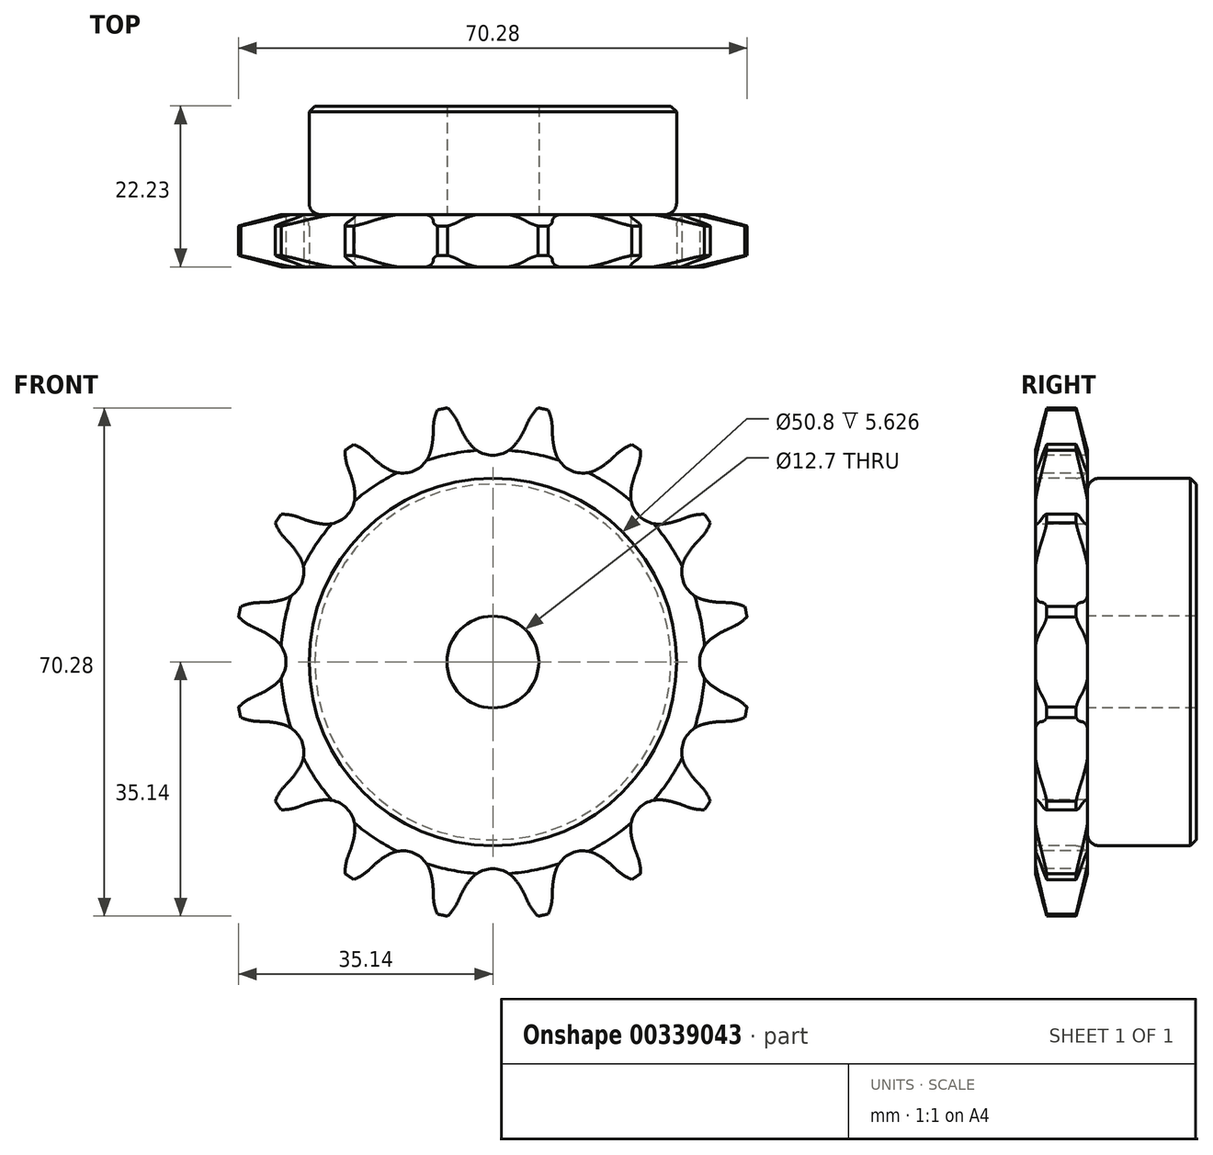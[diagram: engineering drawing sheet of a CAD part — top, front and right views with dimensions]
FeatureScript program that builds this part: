
annotation { "Feature Type Name" : "Feature", "Feature Type Description" : "" }
export const myFeature = defineFeature(function(context is Context, id is Id, definition is map)
    precondition{}
    {
        {
            var Q0;
            Q0=qCreatedBy(makeId("Right.planeOp"),FACE);
            var sketch = newSketch(context, id + "F0", { "sketchPlane" : qUnion([Q0])});
            skLineSegment(sketch, "E0", {"start": v(0, 0) * mm, "end": v(22.23, 0) * mm});
            skLineSegment(sketch, "E1.bottom", {"start": v(0, 6.35) * mm, "end": v(7.21, 6.35) * mm});
            skLineSegment(sketch, "E1.top", {"start": v(0, 35.69) * mm, "end": v(7.21, 35.69) * mm});
            skLineSegment(sketch, "E1.left", {"start": v(0, 6.35) * mm, "end": v(0, 35.69) * mm});
            skLineSegment(sketch, "E1.right", {"start": v(7.21, 6.35) * mm, "end": v(7.21, 35.69) * mm});
            skLineSegment(sketch, "E2.bottom", {"start": v(0, 6.35) * mm, "end": v(22.23, 6.35) * mm});
            skLineSegment(sketch, "E2.top", {"start": v(0, 25.4) * mm, "end": v(22.23, 25.4) * mm});
            skLineSegment(sketch, "E2.left", {"start": v(0, 6.35) * mm, "end": v(0, 25.4) * mm});
            skLineSegment(sketch, "E2.right", {"start": v(22.23, 6.35) * mm, "end": v(22.22, 25.4) * mm});
            skLineSegment(sketch, "E3.MirrorCS", {"start": v(0, -6.35) * mm, "end": v(7.21, -6.35) * mm});
            skLineSegment(sketch, "E4.MirrorCS", {"start": v(0, -25.4) * mm, "end": v(22.23, -25.4) * mm});
            skLineSegment(sketch, "E5.MirrorCS", {"start": v(0, -6.35) * mm, "end": v(22.23, -6.35) * mm});
            skLineSegment(sketch, "E6.MirrorCS", {"start": v(22.23, -6.35) * mm, "end": v(22.23, -25.4) * mm});
            skLineSegment(sketch, "E7.MirrorCS", {"start": v(7.21, -6.35) * mm, "end": v(7.21, -35.69) * mm});
            skLineSegment(sketch, "E8.MirrorCS", {"start": v(0, -6.35) * mm, "end": v(0, -35.69) * mm});
            skLineSegment(sketch, "E9.MirrorCS", {"start": v(0, -35.69) * mm, "end": v(7.21, -35.69) * mm});
            skLineSegment(sketch, "E10.MirrorCS", {"start": v(0, -6.35) * mm, "end": v(0, -25.4) * mm});
            skSolve(sketch);
        }
        {
            var Q0;
            {var subQ5=sQuery(id+"F0.wireOp",EDGE,"E2.right");Q0=makeQuery(id+"F0.imprint","IMPRINT",FACE,{"disambiguationData":[TD([[makeQuery(id+"F0.imprint","IMPRINT",EDGE,{"derivedFrom":subQ5}),1.0]])]});}
            var Q1;
            {var subQ5=sQuery(id+"F0.wireOp",EDGE,"E2.left");Q1=makeQuery(id+"F0.imprint","IMPRINT",FACE,{"disambiguationData":[TD([[makeQuery(id+"F0.imprint","IMPRINT",EDGE,{"derivedFrom":subQ5}),-1.0]])]});}
            var Q2;
            {var subQ0=sQuery(id+"F0.wireOp",EDGE,"E1.top");Q2=makeQuery(id+"F0.imprint","IMPRINT",FACE,{"disambiguationData":[TD([[makeQuery(id+"F0.imprint","IMPRINT",EDGE,{"derivedFrom":subQ0}),-1.0]])]});}
            var Q3;
            Q3=sQuery(id+"F0.wireOp",EDGE,"E0");
            revolve(context, id + "F1", {"entities" : qUnion([Q0, Q1, Q2]), "axis" : qUnion([Q3]), "revolveType" : RevolveType.FULL});
        }
        {
            var Q0;
            Q0=makeQuery(id+"F1.opRevolve","SWEPT_EDGE",EDGE,{"disambiguationData":[OSD([sQuery(id+"F0.wireOp",EDGE,"E1.right"),sQuery(id+"F0.wireOp",EDGE,"E2.top")])]});
            fillet(context, id + "F2", {"entities" : qUnion([Q0]), "radius" : 1.59 * mm, "tangentPropagation" : true, "allowEdgeOverflow" : false});
        }
        {
            var Q0;
            Q0=makeQuery(id+"F1.opRevolve","SWEPT_EDGE",EDGE,{"disambiguationData":[OSD([sQuery(id+"F0.wireOp",EDGE,"E2.top"),sQuery(id+"F0.wireOp",EDGE,"E2.right")])]});
            chamfer(context, id + "F3", {"entities" : qUnion([Q0]), "width" : 0.8 * mm, "tangentPropagation" : true});
        }
        {
            var Q0;
            Q0=makeQuery(id+"F1.opRevolve","SWEPT_EDGE",EDGE,{"disambiguationData":[OSD([sQuery(id+"F0.wireOp",EDGE,"E1.top"),sQuery(id+"F0.wireOp",EDGE,"E1.left")])]});
            var Q1;
            Q1=makeQuery(id+"F1.opRevolve","SWEPT_EDGE",EDGE,{"disambiguationData":[OSD([sQuery(id+"F0.wireOp",EDGE,"E1.top"),sQuery(id+"F0.wireOp",EDGE,"E1.right")])]});
            chamfer(context, id + "F4", {"entities" : qUnion([Q0, Q1]), "chamferType" : ChamferType.TWO_OFFSETS, "width1" : 6.35 * mm, "oppositeDirection" : false, "width2" : 1.57 * mm, "tangentPropagation" : true});
        }
        {
            var Q0;
            Q0=makeQuery(id+"F1.opRevolve","SWEPT_FACE",FACE,{"disambiguationData":[OSD([sQuery(id+"F0.wireOp",EDGE,"E1.left"),sQuery(id+"F0.wireOp",EDGE,"E2.left")])]});
            var sketch = newSketch(context, id + "F5", { "sketchPlane" : qUnion([Q0])});
            skCircle(sketch, "E11", {"center": v(0, 0) * mm, "radius": 32.55 * mm, "construction": true});
            skLineSegment(sketch, "E12", {"start": v(0, 0) * mm, "end": v(0, 32.55) * mm, "construction": true});
            skLineSegment(sketch, "E13", {"start": v(47.22, 32.55) * mm, "end": v(0, 32.55) * mm, "construction": true});
            skLineSegment(sketch, "E14", {"start": v(0, 32.55) * mm, "end": v(5, 36.56) * mm, "construction": true});
            skLineSegment(sketch, "E15", {"start": v(5, 36.56) * mm, "end": v(-4.46, 32.3) * mm, "construction": true});
            skLineSegment(sketch, "E16", {"start": v(-4.46, 32.3) * mm, "end": v(-4.82, 33.1) * mm});
            skLineSegment(sketch, "E17", {"start": v(0, 0) * mm, "end": v(-7.13, 35.85) * mm, "construction": true});
            skArc(sketch, "E18", {"start": v(-7.13, 35.85) * mm, "mid": v(-15.87, 26.15) * mm, "end": v(-4.82, 33.1) * mm, "construction": true});
            skArc(sketch, "E19", {"start": v(-4.82, 33.1) * mm, "mid": v(-5.78, 34.63) * mm, "end": v(-7.13, 35.85) * mm});
            skLineSegment(sketch, "E20", {"start": v(-4.82, 33.1) * mm, "end": v(-4.82, 33.1) * mm});
            skLineSegment(sketch, "E21", {"start": v(-4.46, 32.3) * mm, "end": v(-4.46, 32.3) * mm});
            skArc(sketch, "E22", {"start": v(-3.1, 30.07) * mm, "mid": v(13.83, 41.97) * mm, "end": v(-4.46, 32.3) * mm, "construction": true});
            skArc(sketch, "E23.MirrorCS", {"start": v(4.82, 33.1) * mm, "mid": v(5.78, 34.63) * mm, "end": v(7.13, 35.85) * mm});
            skArc(sketch, "E24.MirrorCS", {"start": v(4.46, 32.3) * mm, "mid": v(3.84, 31.14) * mm, "end": v(3.1, 30.07) * mm});
            skArc(sketch, "E25", {"start": v(-4.46, 32.3) * mm, "mid": v(-3.84, 31.14) * mm, "end": v(-3.1, 30.07) * mm});
            skLineSegment(sketch, "E26", {"start": v(-4.82, 33.1) * mm, "end": v(-11.63, 48.22) * mm, "construction": true});
            skLineSegment(sketch, "E27.MirrorCS", {"start": v(4.46, 32.3) * mm, "end": v(4.82, 33.1) * mm});
            skArc(sketch, "E28", {"start": v(3.1, 30.07) * mm, "mid": v(0, 36.51) * mm, "end": v(-3.1, 30.07) * mm, "construction": true});
            skArc(sketch, "E29", {"start": v(-3.1, 30.07) * mm, "mid": v(0, 28.59) * mm, "end": v(3.1, 30.07) * mm});
            skLineSegment(sketch, "E30.1.0", {"start": v(-16.48, 28.14) * mm, "end": v(-17.12, 28.74) * mm});
            skArc(sketch, "E30.1.1", {"start": v(-17.12, 28.74) * mm, "mid": v(-18.6, 29.79) * mm, "end": v(-20.3, 30.4) * mm});
            skArc(sketch, "E30.1.2", {"start": v(-14.36, 26.6) * mm, "mid": v(-10.94, 26.41) * mm, "end": v(-8.65, 28.96) * mm});
            skArc(sketch, "E30.1.3", {"start": v(-16.48, 28.14) * mm, "mid": v(-15.47, 27.3) * mm, "end": v(-14.36, 26.6) * mm});
            skArc(sketch, "E30.1.4", {"start": v(-8.24, 31.55) * mm, "mid": v(-8.37, 30.24) * mm, "end": v(-8.65, 28.96) * mm});
            skLineSegment(sketch, "E30.1.5", {"start": v(-8.24, 31.55) * mm, "end": v(-8.22, 32.42) * mm});
            skArc(sketch, "E30.1.6", {"start": v(-8.22, 32.42) * mm, "mid": v(-7.91, 34.21) * mm, "end": v(-7.13, 35.85) * mm});
            skLineSegment(sketch, "E30.2.0", {"start": v(-26, 19.69) * mm, "end": v(-26.8, 20) * mm});
            skArc(sketch, "E30.2.1", {"start": v(-26.8, 20) * mm, "mid": v(-28.58, 20.4) * mm, "end": v(-30.4, 20.3) * mm});
            skArc(sketch, "E30.2.2", {"start": v(-23.45, 19.08) * mm, "mid": v(-20.21, 20.21) * mm, "end": v(-19.08, 23.45) * mm});
            skArc(sketch, "E30.2.3", {"start": v(-26, 19.69) * mm, "mid": v(-24.74, 19.3) * mm, "end": v(-23.45, 19.08) * mm});
            skArc(sketch, "E30.2.4", {"start": v(-19.69, 26) * mm, "mid": v(-19.3, 24.74) * mm, "end": v(-19.08, 23.45) * mm});
            skLineSegment(sketch, "E30.2.5", {"start": v(-19.69, 26) * mm, "end": v(-20, 26.8) * mm});
            skArc(sketch, "E30.2.6", {"start": v(-20, 26.8) * mm, "mid": v(-20.4, 28.58) * mm, "end": v(-20.3, 30.4) * mm});
            skLineSegment(sketch, "E30.3.0", {"start": v(-31.55, 8.24) * mm, "end": v(-32.42, 8.22) * mm});
            skArc(sketch, "E30.3.1", {"start": v(-32.42, 8.22) * mm, "mid": v(-34.21, 7.91) * mm, "end": v(-35.85, 7.13) * mm});
            skArc(sketch, "E30.3.2", {"start": v(-28.96, 8.65) * mm, "mid": v(-26.41, 10.94) * mm, "end": v(-26.6, 14.36) * mm});
            skArc(sketch, "E30.3.3", {"start": v(-31.55, 8.24) * mm, "mid": v(-30.24, 8.37) * mm, "end": v(-28.96, 8.65) * mm});
            skArc(sketch, "E30.3.4", {"start": v(-28.14, 16.48) * mm, "mid": v(-27.3, 15.47) * mm, "end": v(-26.6, 14.36) * mm});
            skLineSegment(sketch, "E30.3.5", {"start": v(-28.14, 16.48) * mm, "end": v(-28.74, 17.12) * mm});
            skArc(sketch, "E30.3.6", {"start": v(-28.74, 17.12) * mm, "mid": v(-29.79, 18.6) * mm, "end": v(-30.4, 20.3) * mm});
            skLineSegment(sketch, "E30.4.0", {"start": v(-32.3, -4.46) * mm, "end": v(-33.1, -4.82) * mm});
            skArc(sketch, "E30.4.1", {"start": v(-33.1, -4.82) * mm, "mid": v(-34.63, -5.78) * mm, "end": v(-35.85, -7.13) * mm});
            skArc(sketch, "E30.4.2", {"start": v(-30.07, -3.1) * mm, "mid": v(-28.59, 0) * mm, "end": v(-30.07, 3.1) * mm});
            skArc(sketch, "E30.4.3", {"start": v(-32.3, -4.46) * mm, "mid": v(-31.14, -3.84) * mm, "end": v(-30.07, -3.1) * mm});
            skArc(sketch, "E30.4.4", {"start": v(-32.3, 4.46) * mm, "mid": v(-31.14, 3.84) * mm, "end": v(-30.07, 3.1) * mm});
            skLineSegment(sketch, "E30.4.5", {"start": v(-32.3, 4.46) * mm, "end": v(-33.1, 4.82) * mm});
            skArc(sketch, "E30.4.6", {"start": v(-33.1, 4.82) * mm, "mid": v(-34.63, 5.78) * mm, "end": v(-35.85, 7.13) * mm});
            skLineSegment(sketch, "E30.5.0", {"start": v(-28.14, -16.48) * mm, "end": v(-28.74, -17.12) * mm});
            skArc(sketch, "E30.5.1", {"start": v(-28.74, -17.12) * mm, "mid": v(-29.79, -18.6) * mm, "end": v(-30.4, -20.3) * mm});
            skArc(sketch, "E30.5.2", {"start": v(-26.6, -14.36) * mm, "mid": v(-26.41, -10.94) * mm, "end": v(-28.96, -8.65) * mm});
            skArc(sketch, "E30.5.3", {"start": v(-28.14, -16.48) * mm, "mid": v(-27.3, -15.47) * mm, "end": v(-26.6, -14.36) * mm});
            skArc(sketch, "E30.5.4", {"start": v(-31.55, -8.24) * mm, "mid": v(-30.24, -8.37) * mm, "end": v(-28.96, -8.65) * mm});
            skLineSegment(sketch, "E30.5.5", {"start": v(-31.55, -8.24) * mm, "end": v(-32.42, -8.22) * mm});
            skArc(sketch, "E30.5.6", {"start": v(-32.42, -8.22) * mm, "mid": v(-34.21, -7.91) * mm, "end": v(-35.85, -7.13) * mm});
            skLineSegment(sketch, "E30.6.0", {"start": v(-19.69, -26) * mm, "end": v(-20, -26.8) * mm});
            skArc(sketch, "E30.6.1", {"start": v(-20, -26.8) * mm, "mid": v(-20.4, -28.58) * mm, "end": v(-20.3, -30.4) * mm});
            skArc(sketch, "E30.6.2", {"start": v(-19.08, -23.45) * mm, "mid": v(-20.21, -20.21) * mm, "end": v(-23.45, -19.08) * mm});
            skArc(sketch, "E30.6.3", {"start": v(-19.69, -26) * mm, "mid": v(-19.3, -24.74) * mm, "end": v(-19.08, -23.45) * mm});
            skArc(sketch, "E30.6.4", {"start": v(-26, -19.69) * mm, "mid": v(-24.74, -19.3) * mm, "end": v(-23.45, -19.08) * mm});
            skLineSegment(sketch, "E30.6.5", {"start": v(-26, -19.69) * mm, "end": v(-26.8, -20) * mm});
            skArc(sketch, "E30.6.6", {"start": v(-26.8, -20) * mm, "mid": v(-28.58, -20.4) * mm, "end": v(-30.4, -20.3) * mm});
            skLineSegment(sketch, "E30.7.0", {"start": v(-8.24, -31.55) * mm, "end": v(-8.22, -32.42) * mm});
            skArc(sketch, "E30.7.1", {"start": v(-8.22, -32.42) * mm, "mid": v(-7.91, -34.21) * mm, "end": v(-7.13, -35.85) * mm});
            skArc(sketch, "E30.7.2", {"start": v(-8.65, -28.96) * mm, "mid": v(-10.94, -26.41) * mm, "end": v(-14.36, -26.6) * mm});
            skArc(sketch, "E30.7.3", {"start": v(-8.24, -31.55) * mm, "mid": v(-8.37, -30.24) * mm, "end": v(-8.65, -28.96) * mm});
            skArc(sketch, "E30.7.4", {"start": v(-16.48, -28.14) * mm, "mid": v(-15.47, -27.3) * mm, "end": v(-14.36, -26.6) * mm});
            skLineSegment(sketch, "E30.7.5", {"start": v(-16.48, -28.14) * mm, "end": v(-17.12, -28.74) * mm});
            skArc(sketch, "E30.7.6", {"start": v(-17.12, -28.74) * mm, "mid": v(-18.6, -29.79) * mm, "end": v(-20.3, -30.4) * mm});
            skLineSegment(sketch, "E30.8.0", {"start": v(4.46, -32.3) * mm, "end": v(4.82, -33.1) * mm});
            skArc(sketch, "E30.8.1", {"start": v(4.82, -33.1) * mm, "mid": v(5.78, -34.63) * mm, "end": v(7.13, -35.85) * mm});
            skArc(sketch, "E30.8.2", {"start": v(3.1, -30.07) * mm, "mid": v(0, -28.59) * mm, "end": v(-3.1, -30.07) * mm});
            skArc(sketch, "E30.8.3", {"start": v(4.46, -32.3) * mm, "mid": v(3.84, -31.14) * mm, "end": v(3.1, -30.07) * mm});
            skArc(sketch, "E30.8.4", {"start": v(-4.46, -32.3) * mm, "mid": v(-3.84, -31.14) * mm, "end": v(-3.1, -30.07) * mm});
            skLineSegment(sketch, "E30.8.5", {"start": v(-4.46, -32.3) * mm, "end": v(-4.82, -33.1) * mm});
            skArc(sketch, "E30.8.6", {"start": v(-4.82, -33.1) * mm, "mid": v(-5.78, -34.63) * mm, "end": v(-7.13, -35.85) * mm});
            skLineSegment(sketch, "E30.9.0", {"start": v(16.48, -28.14) * mm, "end": v(17.12, -28.74) * mm});
            skArc(sketch, "E30.9.1", {"start": v(17.12, -28.74) * mm, "mid": v(18.6, -29.79) * mm, "end": v(20.3, -30.4) * mm});
            skArc(sketch, "E30.9.2", {"start": v(14.36, -26.6) * mm, "mid": v(10.94, -26.41) * mm, "end": v(8.65, -28.96) * mm});
            skArc(sketch, "E30.9.3", {"start": v(16.48, -28.14) * mm, "mid": v(15.47, -27.3) * mm, "end": v(14.36, -26.6) * mm});
            skArc(sketch, "E30.9.4", {"start": v(8.24, -31.55) * mm, "mid": v(8.37, -30.24) * mm, "end": v(8.65, -28.96) * mm});
            skLineSegment(sketch, "E30.9.5", {"start": v(8.24, -31.55) * mm, "end": v(8.22, -32.42) * mm});
            skArc(sketch, "E30.9.6", {"start": v(8.22, -32.42) * mm, "mid": v(7.91, -34.21) * mm, "end": v(7.13, -35.85) * mm});
            skLineSegment(sketch, "E30.10.0", {"start": v(26, -19.69) * mm, "end": v(26.8, -20) * mm});
            skArc(sketch, "E30.10.1", {"start": v(26.8, -20) * mm, "mid": v(28.58, -20.4) * mm, "end": v(30.4, -20.3) * mm});
            skArc(sketch, "E30.10.2", {"start": v(23.45, -19.08) * mm, "mid": v(20.21, -20.21) * mm, "end": v(19.08, -23.45) * mm});
            skArc(sketch, "E30.10.3", {"start": v(26, -19.69) * mm, "mid": v(24.74, -19.3) * mm, "end": v(23.45, -19.08) * mm});
            skArc(sketch, "E30.10.4", {"start": v(19.69, -26) * mm, "mid": v(19.3, -24.74) * mm, "end": v(19.08, -23.45) * mm});
            skLineSegment(sketch, "E30.10.5", {"start": v(19.69, -26) * mm, "end": v(20, -26.8) * mm});
            skArc(sketch, "E30.10.6", {"start": v(20, -26.8) * mm, "mid": v(20.4, -28.58) * mm, "end": v(20.3, -30.4) * mm});
            skLineSegment(sketch, "E30.11.0", {"start": v(31.55, -8.24) * mm, "end": v(32.42, -8.22) * mm});
            skArc(sketch, "E30.11.1", {"start": v(32.42, -8.22) * mm, "mid": v(34.21, -7.91) * mm, "end": v(35.85, -7.13) * mm});
            skArc(sketch, "E30.11.2", {"start": v(28.96, -8.65) * mm, "mid": v(26.41, -10.94) * mm, "end": v(26.6, -14.36) * mm});
            skArc(sketch, "E30.11.3", {"start": v(31.55, -8.24) * mm, "mid": v(30.24, -8.37) * mm, "end": v(28.96, -8.65) * mm});
            skArc(sketch, "E30.11.4", {"start": v(28.14, -16.48) * mm, "mid": v(27.3, -15.47) * mm, "end": v(26.6, -14.36) * mm});
            skLineSegment(sketch, "E30.11.5", {"start": v(28.14, -16.48) * mm, "end": v(28.74, -17.12) * mm});
            skArc(sketch, "E30.11.6", {"start": v(28.74, -17.12) * mm, "mid": v(29.79, -18.6) * mm, "end": v(30.4, -20.3) * mm});
            skLineSegment(sketch, "E30.12.0", {"start": v(32.3, 4.46) * mm, "end": v(33.1, 4.82) * mm});
            skArc(sketch, "E30.12.1", {"start": v(33.1, 4.82) * mm, "mid": v(34.63, 5.78) * mm, "end": v(35.85, 7.13) * mm});
            skArc(sketch, "E30.12.2", {"start": v(30.07, 3.1) * mm, "mid": v(28.59, 0) * mm, "end": v(30.07, -3.1) * mm});
            skArc(sketch, "E30.12.3", {"start": v(32.3, 4.46) * mm, "mid": v(31.14, 3.84) * mm, "end": v(30.07, 3.1) * mm});
            skArc(sketch, "E30.12.4", {"start": v(32.3, -4.46) * mm, "mid": v(31.14, -3.84) * mm, "end": v(30.07, -3.1) * mm});
            skLineSegment(sketch, "E30.12.5", {"start": v(32.3, -4.46) * mm, "end": v(33.1, -4.82) * mm});
            skArc(sketch, "E30.12.6", {"start": v(33.1, -4.82) * mm, "mid": v(34.63, -5.78) * mm, "end": v(35.85, -7.13) * mm});
            skLineSegment(sketch, "E30.13.0", {"start": v(28.14, 16.48) * mm, "end": v(28.74, 17.12) * mm});
            skArc(sketch, "E30.13.1", {"start": v(28.74, 17.12) * mm, "mid": v(29.79, 18.6) * mm, "end": v(30.4, 20.3) * mm});
            skArc(sketch, "E30.13.2", {"start": v(26.6, 14.36) * mm, "mid": v(26.41, 10.94) * mm, "end": v(28.96, 8.65) * mm});
            skArc(sketch, "E30.13.3", {"start": v(28.14, 16.48) * mm, "mid": v(27.3, 15.47) * mm, "end": v(26.6, 14.36) * mm});
            skArc(sketch, "E30.13.4", {"start": v(31.55, 8.24) * mm, "mid": v(30.24, 8.37) * mm, "end": v(28.96, 8.65) * mm});
            skLineSegment(sketch, "E30.13.5", {"start": v(31.55, 8.24) * mm, "end": v(32.42, 8.22) * mm});
            skArc(sketch, "E30.13.6", {"start": v(32.42, 8.22) * mm, "mid": v(34.21, 7.91) * mm, "end": v(35.85, 7.13) * mm});
            skLineSegment(sketch, "E30.14.0", {"start": v(19.69, 26) * mm, "end": v(20, 26.8) * mm});
            skArc(sketch, "E30.14.1", {"start": v(20, 26.8) * mm, "mid": v(20.4, 28.58) * mm, "end": v(20.3, 30.4) * mm});
            skArc(sketch, "E30.14.2", {"start": v(19.08, 23.45) * mm, "mid": v(20.21, 20.21) * mm, "end": v(23.45, 19.08) * mm});
            skArc(sketch, "E30.14.3", {"start": v(19.69, 26) * mm, "mid": v(19.3, 24.74) * mm, "end": v(19.08, 23.45) * mm});
            skArc(sketch, "E30.14.4", {"start": v(26, 19.69) * mm, "mid": v(24.74, 19.3) * mm, "end": v(23.45, 19.08) * mm});
            skLineSegment(sketch, "E30.14.5", {"start": v(26, 19.69) * mm, "end": v(26.8, 20) * mm});
            skArc(sketch, "E30.14.6", {"start": v(26.8, 20) * mm, "mid": v(28.58, 20.4) * mm, "end": v(30.4, 20.3) * mm});
            skLineSegment(sketch, "E30.15.0", {"start": v(8.24, 31.55) * mm, "end": v(8.22, 32.42) * mm});
            skArc(sketch, "E30.15.1", {"start": v(8.22, 32.42) * mm, "mid": v(7.91, 34.21) * mm, "end": v(7.13, 35.85) * mm});
            skArc(sketch, "E30.15.2", {"start": v(8.65, 28.96) * mm, "mid": v(10.94, 26.41) * mm, "end": v(14.36, 26.6) * mm});
            skArc(sketch, "E30.15.3", {"start": v(8.24, 31.55) * mm, "mid": v(8.37, 30.24) * mm, "end": v(8.65, 28.96) * mm});
            skArc(sketch, "E30.15.4", {"start": v(16.48, 28.14) * mm, "mid": v(15.47, 27.3) * mm, "end": v(14.36, 26.6) * mm});
            skLineSegment(sketch, "E30.15.5", {"start": v(16.48, 28.14) * mm, "end": v(17.12, 28.74) * mm});
            skArc(sketch, "E30.15.6", {"start": v(17.12, 28.74) * mm, "mid": v(18.6, 29.79) * mm, "end": v(20.3, 30.4) * mm});
            skSolve(sketch);
        }
        {
            var Q0;
            Q0=qSketchRegion(id+"F5",true);
            extrude(context, id + "F6", {"entities" : qUnion([Q0]), "operationType" : NewBodyOperationType.INTERSECT, "endBound" : BoundingType.THROUGH_ALL, "oppositeDirection" : true, "depth" : 25.4 * mm});
        }
    });
